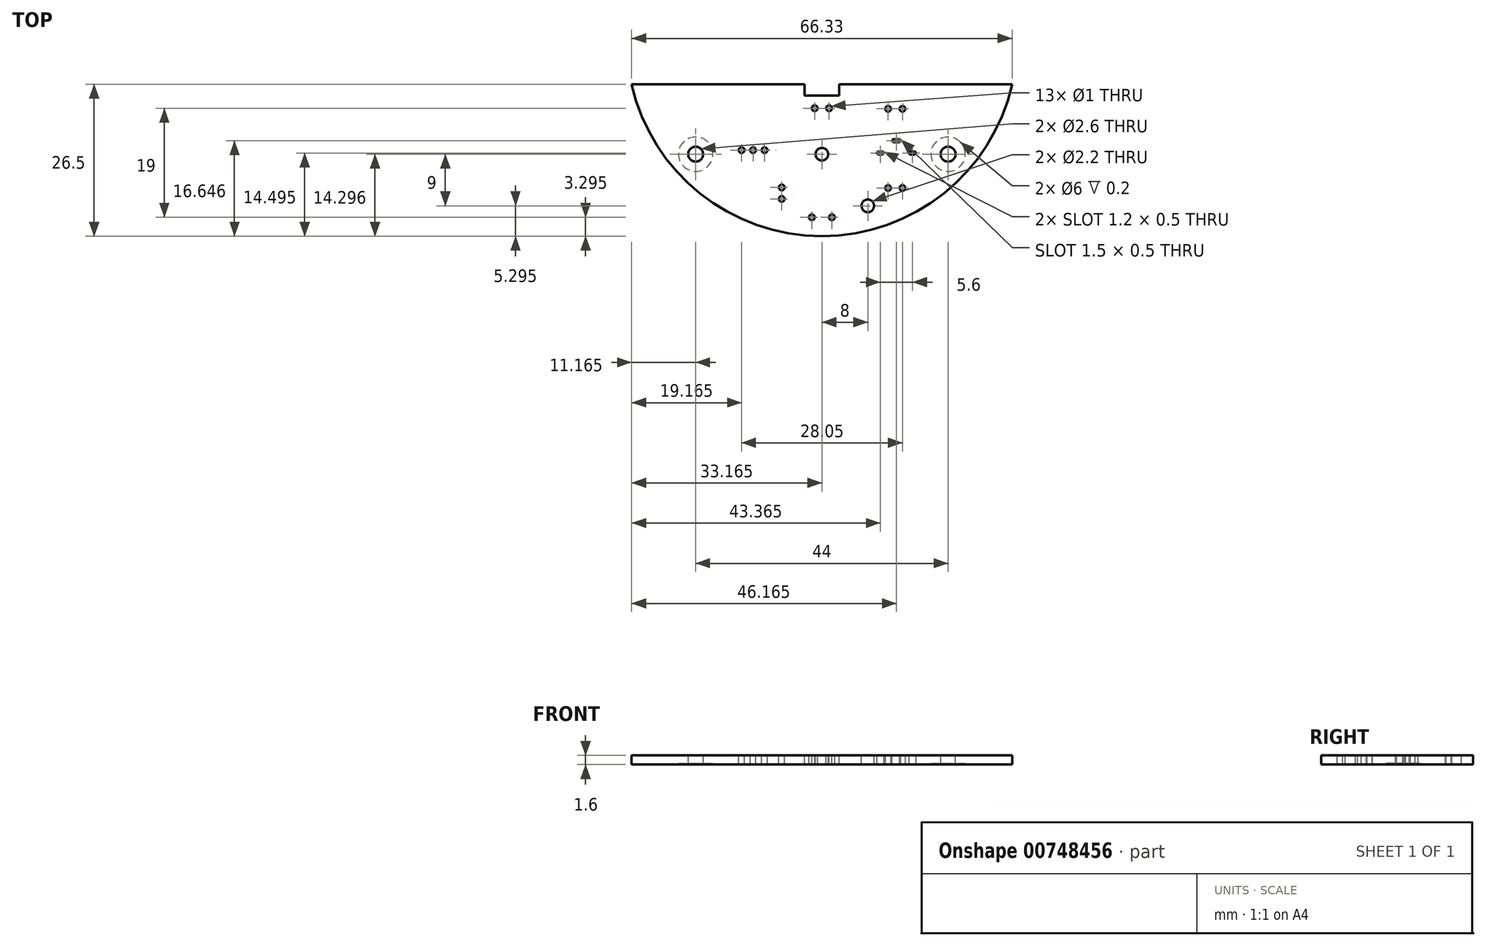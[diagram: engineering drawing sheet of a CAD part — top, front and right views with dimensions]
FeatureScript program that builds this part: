
annotation { "Feature Type Name" : "Feature", "Feature Type Description" : "" }
export const myFeature = defineFeature(function(context is Context, id is Id, definition is map)
    precondition{}
    {
        {
            var Q0;
            Q0=qCreatedBy(makeId("Top.planeOp"),FACE);
            var sketch = newSketch(context, id + "F0", { "sketchPlane" : qUnion([Q0])});
            skLineSegment(sketch, "E0.bottom", {"start": v(6.37, 29.29) * mm, "end": v(70.72, 29.29) * mm, "construction": true});
            skPoint(sketch, "E1.middle", {"position": v(38.54, 20.77) * mm});
            skPoint(sketch, "E2.orphan", {"position": v(18.04, 25.29) * mm});
            skPoint(sketch, "E3.orphan", {"position": v(59.04, 25.29) * mm});
            skArc(sketch, "E4", {"start": v(5.38, 32.79) * mm, "mid": v(38.54, 6.29) * mm, "end": v(71.7, 32.79) * mm});
            skLineSegment(sketch, "E5.0", {"start": v(5.38, 32.79) * mm, "end": v(71.7, 32.79) * mm});
            skLineSegment(sketch, "E6.0", {"start": v(5.38, 31.29) * mm, "end": v(71.7, 31.29) * mm, "construction": true});
            skSolve(sketch);
        }
        {
            var Q0;
            Q0=qSketchRegion(id+"F0",true);
            extrude(context, id + "F1", {"entities" : qUnion([Q0]), "depth" : 1.6 * mm});
        }
        {
            var Q0;
            Q0=makeQuery(id+"F1.opExtrude","CAP_FACE",FACE,{"disambiguationData":[OSD([sQuery(id+"F0.wireOp",EDGE,"E4"),sQuery(id+"F0.wireOp",EDGE,"E5.0")])],"isStart":false});
            var sketch = newSketch(context, id + "F2", { "sketchPlane" : qUnion([Q0])});
            skCircle(sketch, "E7", {"center": v(16.54, 20.59) * mm, "radius": 1.3 * mm});
            skLineSegment(sketch, "E8", {"start": v(38.54, 22.42) * mm, "end": v(38.54, 32.79) * mm, "construction": true});
            skCircle(sketch, "E9.MirrorC", {"center": v(60.54, 20.59) * mm, "radius": 1.3 * mm});
            skCircle(sketch, "E10", {"center": v(38.54, 20.59) * mm, "radius": 1.1 * mm});
            skCircle(sketch, "E11", {"center": v(46.54, 11.59) * mm, "radius": 1.1 * mm});
            skSolve(sketch);
        }
        {
            var Q0;
            Q0=qSketchRegion(id+"F2",true);
            extrude(context, id + "F3", {"entities" : qUnion([Q0]), "operationType" : NewBodyOperationType.REMOVE, "oppositeDirection" : true, "depth" : 3 * mm, "offsetDistance" : 25 * mm});
        }
        {
            var Q0;
            Q0=makeQuery(id+"F1.opExtrude","CAP_FACE",FACE,{"disambiguationData":[OSD([sQuery(id+"F0.wireOp",EDGE,"E4"),sQuery(id+"F0.wireOp",EDGE,"E5.0")])],"isStart":false});
            var sketch = newSketch(context, id + "F4", { "sketchPlane" : qUnion([Q0])});
            skCircle(sketch, "E12", {"center": v(24.54, 21.29) * mm, "radius": 0.5 * mm});
            skLineSegment(sketch, "E13", {"start": v(38.54, 22.32) * mm, "end": v(38.54, 32.79) * mm, "construction": true});
            skCircle(sketch, "E14.1.0.0", {"center": v(26.54, 21.29) * mm, "radius": 0.5 * mm});
            skLineSegment(sketch, "E14.direction1", {"start": v(24.54, 21.29) * mm, "end": v(26.54, 21.29) * mm, "construction": true});
            skCircle(sketch, "E15.0.2.0", {"center": v(28.54, 21.29) * mm, "radius": 0.5 * mm});
            skSolve(sketch);
        }
        {
            var Q0;
            Q0=makeQuery(id+"F1.opExtrude","CAP_FACE",FACE,{"disambiguationData":[OSD([sQuery(id+"F0.wireOp",EDGE,"E4"),sQuery(id+"F0.wireOp",EDGE,"E5.0")])],"isStart":false});
            var sketch = newSketch(context, id + "F5", { "sketchPlane" : qUnion([Q0])});
            skLineSegment(sketch, "E16", {"start": v(51.54, 14.1) * mm, "end": v(51.54, 27.42) * mm, "construction": true});
            skLineSegment(sketch, "E17", {"start": v(38.54, 6.29) * mm, "end": v(38.54, 24.04) * mm, "construction": true});
            skLineSegment(sketch, "E18", {"start": v(48.4, 20.79) * mm, "end": v(49.1, 20.79) * mm, "construction": true});
            skLineSegment(sketch, "E19", {"start": v(48.74, 20.79) * mm, "end": v(48.74, 23.97) * mm, "construction": true});
            skLineSegment(sketch, "E20", {"start": v(51.04, 22.94) * mm, "end": v(52.04, 22.94) * mm, "construction": true});
            skLineSegment(sketch, "E21", {"start": v(51.54, 22.94) * mm, "end": v(51.54, 19.92) * mm, "construction": true});
            skArc(sketch, "E22.0.startCap", {"start": v(51.04, 22.69) * mm, "mid": v(50.8, 22.94) * mm, "end": v(51.04, 23.19) * mm});
            skArc(sketch, "E22.0.endCap", {"start": v(52.04, 23.19) * mm, "mid": v(52.3, 22.94) * mm, "end": v(52.04, 22.69) * mm});
            skLineSegment(sketch, "E22.0.left", {"start": v(51.04, 23.19) * mm, "end": v(52.04, 23.19) * mm});
            skLineSegment(sketch, "E22.0.right", {"start": v(51.04, 22.69) * mm, "end": v(52.04, 22.69) * mm});
            skLineSegment(sketch, "E23", {"start": v(50.45, 21.94) * mm, "end": v(53.65, 21.94) * mm, "construction": true});
            skArc(sketch, "E24.0.startCap", {"start": v(49.1, 21.04) * mm, "mid": v(49.34, 20.79) * mm, "end": v(49.1, 20.54) * mm});
            skArc(sketch, "E24.0.endCap", {"start": v(48.4, 20.54) * mm, "mid": v(48.14, 20.79) * mm, "end": v(48.4, 21.04) * mm});
            skLineSegment(sketch, "E24.0.left", {"start": v(48.4, 20.54) * mm, "end": v(49.1, 20.54) * mm});
            skLineSegment(sketch, "E24.0.right", {"start": v(48.4, 21.04) * mm, "end": v(49.1, 21.04) * mm});
            skArc(sketch, "E25.MirrorCS", {"start": v(54.7, 20.54) * mm, "mid": v(54.94, 20.79) * mm, "end": v(54.7, 21.04) * mm});
            skLineSegment(sketch, "E26.MirrorCS", {"start": v(54.7, 20.54) * mm, "end": v(54, 20.54) * mm});
            skLineSegment(sketch, "E27.MirrorCS", {"start": v(54.7, 21.04) * mm, "end": v(54, 21.04) * mm});
            skArc(sketch, "E28.MirrorCS", {"start": v(54, 21.04) * mm, "mid": v(53.74, 20.79) * mm, "end": v(54, 20.54) * mm});
            skSolve(sketch);
        }
        {
            var Q0;
            Q0=makeQuery(id+"F1.opExtrude","CAP_FACE",FACE,{"disambiguationData":[OSD([sQuery(id+"F0.wireOp",EDGE,"E0.bottom"),sQuery(id+"F0.wireOp",EDGE,"E4")])],"isStart":false});
            var sketch = newSketch(context, id + "F6", { "sketchPlane" : qUnion([Q0])});
            skCircle(sketch, "E29", {"center": v(50.1, 14.69) * mm, "radius": 0.5 * mm});
            skLineSegment(sketch, "E30.direction1", {"start": v(50.1, 14.69) * mm, "end": v(52.6, 14.69) * mm, "construction": true});
            skLineSegment(sketch, "E31", {"start": v(38.54, 6.29) * mm, "end": v(38.54, 17.65) * mm, "construction": true});
            skLineSegment(sketch, "E32", {"start": v(51.34, 14.69) * mm, "end": v(51.34, 23.7) * mm, "construction": true});
            skCircle(sketch, "E33", {"center": v(52.6, 14.69) * mm, "radius": 0.5 * mm});
            skCircle(sketch, "E34", {"center": v(50.1, 28.49) * mm, "radius": 0.5 * mm});
            skCircle(sketch, "E35", {"center": v(52.6, 28.49) * mm, "radius": 0.5 * mm});
            skSolve(sketch);
        }
        {
            var Q0;
            Q0=makeQuery(id+"F1.opExtrude","CAP_FACE",FACE,{"disambiguationData":[OSD([sQuery(id+"F0.wireOp",EDGE,"E0.bottom"),sQuery(id+"F0.wireOp",EDGE,"E4")])],"isStart":false});
            var sketch = newSketch(context, id + "F7", { "sketchPlane" : qUnion([Q0])});
            skCircle(sketch, "E36", {"center": v(37.3, 28.59) * mm, "radius": 0.5 * mm});
            skCircle(sketch, "E37.1.0.0", {"center": v(39.8, 28.59) * mm, "radius": 0.5 * mm});
            skLineSegment(sketch, "E37.direction1", {"start": v(37.3, 28.59) * mm, "end": v(39.8, 28.59) * mm, "construction": true});
            skLineSegment(sketch, "E38", {"start": v(38.54, 15.29) * mm, "end": v(38.54, 32.79) * mm, "construction": true});
            skLineSegment(sketch, "E39", {"start": v(38.54, 26.14) * mm, "end": v(38.54, 28.59) * mm, "construction": true});
            skSolve(sketch);
        }
        {
            var Q0;
            Q0=makeQuery(id+"F1.opExtrude","CAP_FACE",FACE,{"disambiguationData":[OSD([sQuery(id+"F0.wireOp",EDGE,"E0.bottom"),sQuery(id+"F0.wireOp",EDGE,"E4")])],"isStart":false});
            var sketch = newSketch(context, id + "F8", { "sketchPlane" : qUnion([Q0])});
            skCircle(sketch, "E40", {"center": v(36.8, 9.59) * mm, "radius": 0.5 * mm});
            skCircle(sketch, "E41.1.0.0", {"center": v(40.3, 9.59) * mm, "radius": 0.5 * mm});
            skLineSegment(sketch, "E41.direction1", {"start": v(36.8, 9.59) * mm, "end": v(40.3, 9.59) * mm, "construction": true});
            skLineSegment(sketch, "E42", {"start": v(38.54, 32.79) * mm, "end": v(38.54, 9.59) * mm, "construction": true});
            skSolve(sketch);
        }
        {
            var Q0;
            Q0=makeQuery(id+"F1.opExtrude","CAP_FACE",FACE,{"disambiguationData":[OSD([sQuery(id+"F0.wireOp",EDGE,"E0.bottom"),sQuery(id+"F0.wireOp",EDGE,"E4")])],"isStart":false});
            var sketch = newSketch(context, id + "F9", { "sketchPlane" : qUnion([Q0])});
            skCircle(sketch, "E43", {"center": v(31.54, 12.79) * mm, "radius": 0.5 * mm});
            skCircle(sketch, "E44", {"center": v(31.54, 14.79) * mm, "radius": 0.5 * mm});
            skSolve(sketch);
        }
        {
            var Q0;
            Q0=qSketchRegion(id+"F6",true);
            var Q1;
            Q1=qSketchRegion(id+"F7",true);
            var Q2;
            Q2=qSketchRegion(id+"F8",true);
            var Q3;
            Q3=qSketchRegion(id+"F5",true);
            var Q4;
            Q4=qSketchRegion(id+"F4",true);
            var Q5;
            Q5=qSketchRegion(id+"F9",true);
            extrude(context, id + "F10", {"entities" : qUnion([Q0, Q1, Q2, Q3, Q4, Q5]), "operationType" : NewBodyOperationType.REMOVE, "oppositeDirection" : true, "depth" : 4 * mm, "offsetDistance" : 25 * mm});
        }
        {
            var Q0;
            Q0=makeQuery(id+"F1.opExtrude","CAP_FACE",FACE,{"disambiguationData":[OSD([sQuery(id+"F0.wireOp",EDGE,"E0.bottom"),sQuery(id+"F0.wireOp",EDGE,"E4")])],"isStart":true});
            var sketch = newSketch(context, id + "F11", { "sketchPlane" : qUnion([Q0])});
            skCircle(sketch, "E45", {"center": v(60.54, -20.59) * mm, "radius": 3 * mm});
            skLineSegment(sketch, "E46", {"start": v(38.54, -32.79) * mm, "end": v(38.54, 3.6) * mm, "construction": true});
            skCircle(sketch, "E47.MirrorC", {"center": v(16.54, -20.59) * mm, "radius": 3 * mm});
            skSolve(sketch);
        }
        {
            var Q0;
            Q0=qSketchRegion(id+"F11",true);
            extrude(context, id + "F12", {"entities" : qUnion([Q0]), "operationType" : NewBodyOperationType.REMOVE, "oppositeDirection" : true, "depth" : .2 * mm});
        }
        {
            var Q0;
            Q0=makeQuery(id+"F1.opExtrude","CAP_FACE",FACE,{"disambiguationData":[OSD([sQuery(id+"F0.wireOp",EDGE,"E4"),sQuery(id+"F0.wireOp",EDGE,"E5.0")])],"isStart":false});
            var sketch = newSketch(context, id + "F13", { "sketchPlane" : qUnion([Q0])});
            skLineSegment(sketch, "E48", {"start": v(38.54, 32.79) * mm, "end": v(38.54, 37.88) * mm, "construction": true});
            skLineSegment(sketch, "E49.0", {"start": v(41.54, 32.79) * mm, "end": v(41.54, 37.88) * mm, "construction": true});
            skLineSegment(sketch, "E50.0", {"start": v(35.54, 32.79) * mm, "end": v(35.54, 37.88) * mm, "construction": true});
            skLineSegment(sketch, "E51.bottom", {"start": v(35.54, 32.79) * mm, "end": v(41.54, 32.79) * mm, "construction": true});
            skLineSegment(sketch, "E51.top", {"start": v(35.54, 32.79) * mm, "end": v(41.54, 32.79) * mm, "construction": true});
            skLineSegment(sketch, "E51.left", {"start": v(35.54, 32.79) * mm, "end": v(35.54, 32.79) * mm});
            skLineSegment(sketch, "E51.right", {"start": v(41.54, 32.79) * mm, "end": v(41.54, 32.79) * mm});
            skLineSegment(sketch, "E52.bottom", {"start": v(35.54, 32.79) * mm, "end": v(41.54, 32.79) * mm});
            skLineSegment(sketch, "E52.top", {"start": v(35.54, 30.79) * mm, "end": v(41.54, 30.79) * mm});
            skLineSegment(sketch, "E52.left", {"start": v(35.54, 32.79) * mm, "end": v(35.54, 30.79) * mm});
            skLineSegment(sketch, "E52.right", {"start": v(41.54, 32.79) * mm, "end": v(41.54, 30.79) * mm});
            skSolve(sketch);
        }
        {
            var Q0;
            Q0=qSketchRegion(id+"F13",true);
            extrude(context, id + "F14", {"entities" : qUnion([Q0]), "operationType" : NewBodyOperationType.REMOVE, "oppositeDirection" : true, "depth" : 25 * mm, "offsetDistance" : 25 * mm});
        }
    });
